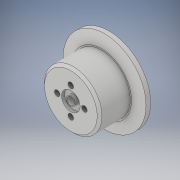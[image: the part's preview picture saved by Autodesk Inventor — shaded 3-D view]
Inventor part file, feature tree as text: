
AUTODESK INVENTOR PART (.ipt)
format: ipt  version: 2019.4 (Build 234330000, 330)  size: 168,960 bytes
history: native  units: in
note: dims shown in document units (in); Inventor stores cm internally (conversion verified against a paired STEP export)
features: sketch x3, extrude x2, hole x1
ambient origin geometry x8: Origin, YZ Plane, XZ Plane, XY Plane, X Axis, Y Axis, Z Axis, Center Point
bodies: Solid1 (feature_tree)
feature tree (6):
  extrude  "Extrusion1"  Depth=1.0in TaperAngle=0.0deg
  extrude  "Extrusion2"  Depth=0.121in
  hole  "Hole1"  [1 undecoded]
  sketch  "Sketch1"  dims[d0=0.2in d1=1.0in d2=0.0in]
  sketch  "Sketch2"  dims[d3=0.241in d5=0.121in]
  sketch  "Sketch3"  dims[d6=0.078in d7=0.0in d12=0.355in d14=0.355in d15=0.355in d16=0.355in d17=0.355in d18=0.502in d19=0.71in d20=0.355in d21=0.145in d22=0.38in d23=0.332in d24=0.25in d25=0.563in d26=0.588in d27=0.8108in]
note: 1 required parameter value undecoded (feature->parameter linkage not recoverable at this tier; creation-order binding heuristic only, values carry confidence <= 0.55)
